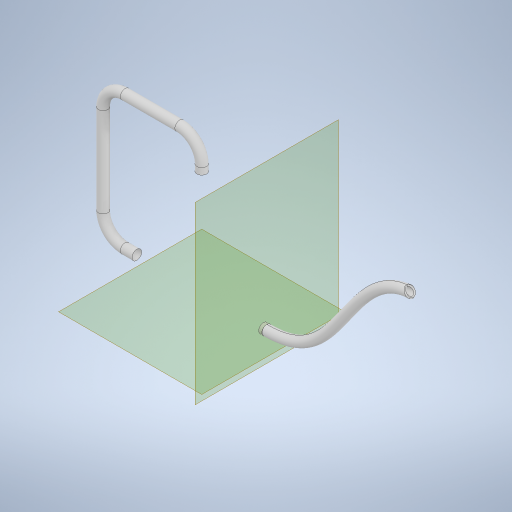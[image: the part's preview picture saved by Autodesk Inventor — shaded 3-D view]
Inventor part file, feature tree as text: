
AUTODESK INVENTOR PART (.ipt)
format: ipt  version: 2024 (Build 280153000, 153)  size: 572,928 bytes
history: native  units: mm
features: sketch x16, extrude x8, fillet x6, plane x6, delete_face x3, sweep x2, revolve x1
ambient origin geometry x8: Origin, YZ Plane, XZ Plane, XY Plane, X Axis, Y Axis, Z Axis, Center Point
bodies: Solid1 (feature_tree), Solid3 (feature_tree)
feature tree (42):
  extrude  "Extrusion1"  Depth=5.0mm TaperAngle=0.0deg
  fillet  "Fillet1"  Radius=2.5mm
  extrude  "Extrusion2"  Depth=95.0mm TaperAngle=0.0deg
  plane  "Work Plane1"
  extrude  "Extrusion3"  Depth=110.0mm
  sketch  "Sketch5"  dims[d9=103.0mm d10=3.5mm d11=0.0mm]
  revolve  "Revolution1"  [1 undecoded]
  extrude  "Extrusion4"  TaperAngle=90.0deg  [1 undecoded]
  sketch  "Sketch8"  dims[d19=11.5mm d20=77.5mm]
  plane  "Work Plane2"
  sketch  "Sketch9"  dims[d21=25.0mm d22=10.0mm d23=3.0mm d24=1.0mm]
  fillet  "Fillet2"  Radius=25.0mm
  fillet  "Fillet3"  Radius=88.0mm
  sketch  "Sketch11"  dims[d25=35.0mm d26=35.0mm]
  extrude  "Extrusion5"  Depth=3.5mm TaperAngle=0.0deg
  sweep  "Sweep1"
  plane  "Work Plane3"
  sketch  "Sketch13"  dims[d30=26.25mm d31=26.25mm]
  plane  "Work Plane4"
  sketch  "Sketch14"  dims[d32=75.0mm]
  sketch  "Sketch16"  dims[d33=8.75mm]
  extrude  "Extrusion7"  Depth=10.0mm
  fillet  "Fillet4"  Radius=3.0mm
  fillet  "Fillet5"  Radius=1.0mm
  sweep  "Sweep2"
  extrude  "Extrusion8"  Depth=10.0mm
  fillet  "Fillet6"  Radius=13.75mm
  plane  "Work Plane5"
  delete_face  "Delete Face1"
  delete_face  "Delete Face2"
  delete_face  "Delete Face3"
  plane  "Work Plane6"
  extrude  "Extrusion9"  Depth=26.25mm
  sketch  "Sketch1"  dims[d0=160.0mm d1=5.0mm d2=0.0mm d3=2.5mm]
  sketch  "Sketch2"  dims[d4=148.0mm d5=95.0mm d6=0.0mm]
  sketch  "Sketch3"  dims[d7=50.0mm d8=110.0mm]
  sketch  "Sketch6"  dims[d12=3.5mm d13=90.0deg d14=25.0mm d15=88.0mm]
  sketch  "Sketch7"  dims[d16=88.0mm d17=3.5mm d18=0.0mm]
  sketch  "Sketch12"  dims[d27=40.0mm d28=10.0mm d29=13.75mm]
  sketch  "Sketch17"  dims[d34=26.25mm]
  sketch  "Sketch18"  dims[d35=26.25mm]
  sketch  "Sketch19"  dims[d36=26.25mm d37=26.25mm d38=26.25mm d39=10.0mm d40=0.5mm d41=0.0mm d42=0.0mm d43=0.0mm d44=-77.5mm d45=75.0mm d46=11.5mm d47=-175.0mm d53=11.5mm d54=7.0mm d64=5.0mm d65=0.0mm d66=2.0mm d67=5.0mm d68=0.0mm d69=0.0mm d70=11.5mm d71=0.0mm d72=1.2mm d73=-5.0mm d74=1.5mm d75=1.25mm d76=15.0mm d77=3.5mm d78=74.035414mm d79=-77.5mm d80=2.25mm d81=4.0mm d82=0.0mm d55=0.872665mm d56=0.5mm d57=0.872665mm d58=0.872665mm d59=0.5mm d60=0.872665mm]
note: 2 required parameter values undecoded (feature->parameter linkage not recoverable at this tier; creation-order binding heuristic only, values carry confidence <= 0.55)